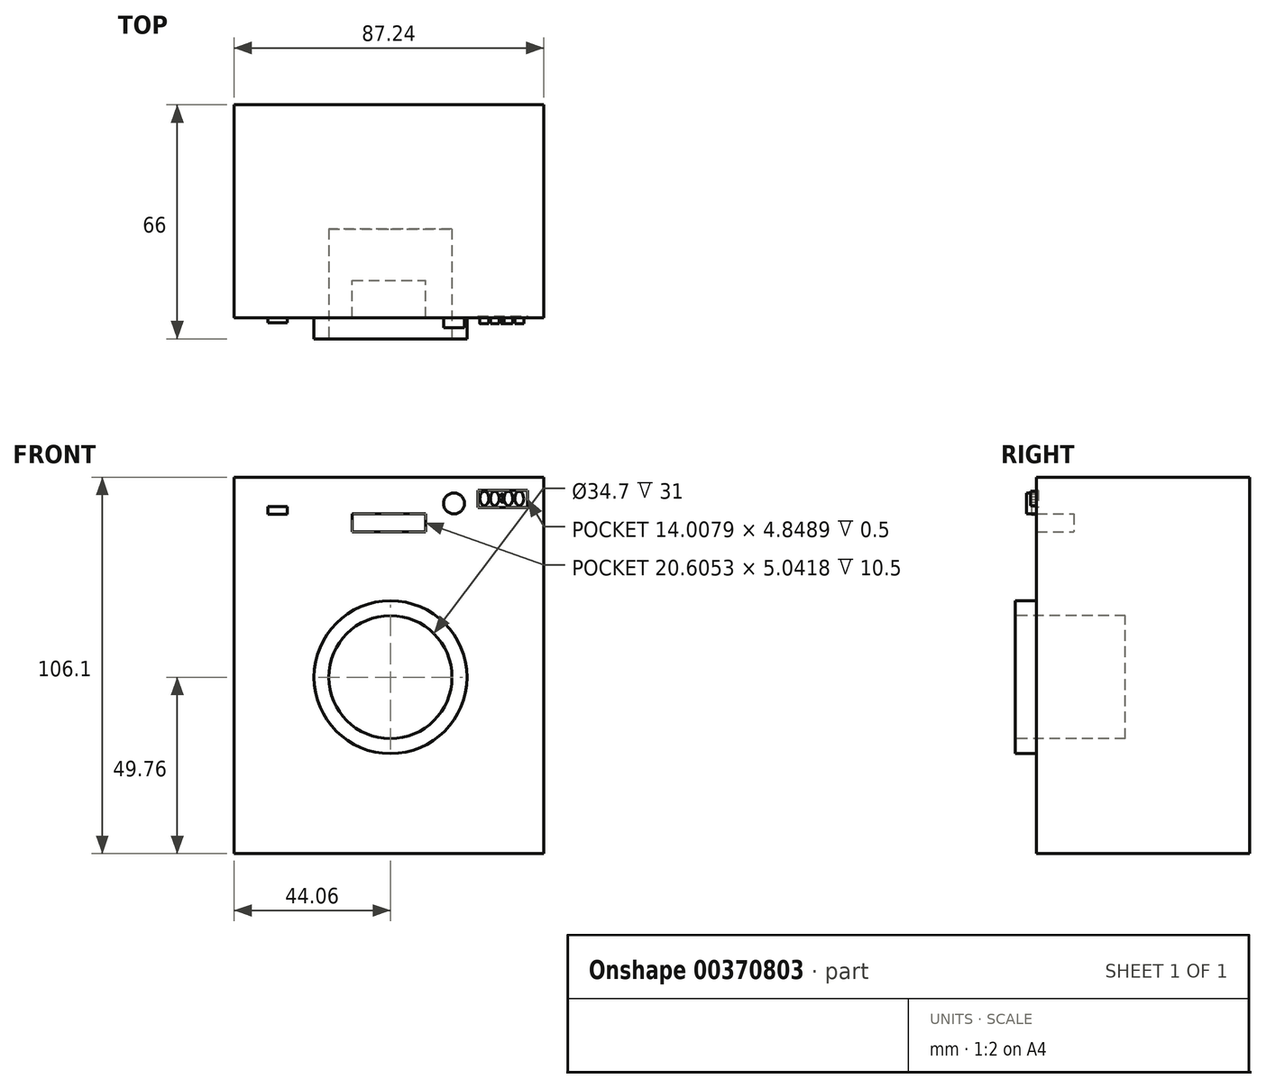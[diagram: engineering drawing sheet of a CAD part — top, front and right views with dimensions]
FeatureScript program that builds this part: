
annotation { "Feature Type Name" : "Feature", "Feature Type Description" : "" }
export const myFeature = defineFeature(function(context is Context, id is Id, definition is map)
    precondition{}
    {
        {
            var Q0;
            Q0=qCreatedBy(makeId("Front.planeOp"),FACE);
            var sketch = newSketch(context, id + "F0", { "sketchPlane" : qUnion([Q0])});
            skLineSegment(sketch, "E0.bottom", {"start": v(-44.06, 56.34) * mm, "end": v(43.18, 56.34) * mm});
            skLineSegment(sketch, "E0.top", {"start": v(-44.06, -49.76) * mm, "end": v(43.18, -49.76) * mm});
            skLineSegment(sketch, "E0.left", {"start": v(-44.06, 56.34) * mm, "end": v(-44.06, -49.76) * mm});
            skLineSegment(sketch, "E0.right", {"start": v(43.18, 56.34) * mm, "end": v(43.18, -49.76) * mm});
            skLineSegment(sketch, "E1.bottom", {"start": v(-10.74, 46.03) * mm, "end": v(9.86, 46.03) * mm});
            skLineSegment(sketch, "E1.top", {"start": v(-10.74, 41) * mm, "end": v(9.86, 41) * mm});
            skLineSegment(sketch, "E1.left", {"start": v(-10.74, 46.03) * mm, "end": v(-10.74, 41) * mm});
            skLineSegment(sketch, "E1.right", {"start": v(9.86, 46.03) * mm, "end": v(9.86, 41) * mm});
            skSolve(sketch);
        }
        {
            var Q0;
            Q0=makeQuery(id+"F0.imprint","IMPRINT",FACE,{"disambiguationData":[TD([[makeQuery(id+"F0.imprint","IMPRINT",EDGE,{"derivedFrom":sQuery(id+"F0.wireOp",EDGE,"E0.bottom")}),-1.0]])]});
            extrude(context, id + "F1", {"entities" : qUnion([Q0]), "depth" : 60 * mm});
        }
        {
            var Q0;
            Q0=makeQuery(id+"F1.opExtrude","CAP_FACE",FACE,{"disambiguationData":[OSD([sQuery(id+"F0.wireOp",EDGE,"E0.bottom"),sQuery(id+"F0.wireOp",EDGE,"E0.top"),sQuery(id+"F0.wireOp",EDGE,"E0.left"),sQuery(id+"F0.wireOp",EDGE,"E0.right"),sQuery(id+"F0.wireOp",EDGE,"E1.bottom"),sQuery(id+"F0.wireOp",EDGE,"E1.top"),sQuery(id+"F0.wireOp",EDGE,"E1.left"),sQuery(id+"F0.wireOp",EDGE,"E1.right")])],"isStart":false});
            var sketch = newSketch(context, id + "F2", { "sketchPlane" : qUnion([Q0])});
            skCircle(sketch, "E2", {"center": v(17.9, 48.98) * mm, "radius": 2.94 * mm});
            skSolve(sketch);
        }
        {
            var Q0;
            Q0=makeQuery(id+"F2.imprint","IMPRINT",FACE,{"disambiguationData":[TD([[makeQuery(id+"F2.imprint","IMPRINT",EDGE,{"derivedFrom":sQuery(id+"F2.wireOp",EDGE,"E2")}),1.0]])]});
            extrude(context, id + "F3", {"entities" : qUnion([Q0]), "operationType" : NewBodyOperationType.ADD, "depth" : 2.9 * mm});
        }
        {
            var Q0;
            Q0=makeQuery(id+"F1.opExtrude","CAP_FACE",FACE,{"disambiguationData":[OSD([sQuery(id+"F0.wireOp",EDGE,"E0.bottom"),sQuery(id+"F0.wireOp",EDGE,"E0.top"),sQuery(id+"F0.wireOp",EDGE,"E0.left"),sQuery(id+"F0.wireOp",EDGE,"E0.right"),sQuery(id+"F0.wireOp",EDGE,"E1.bottom"),sQuery(id+"F0.wireOp",EDGE,"E1.top"),sQuery(id+"F0.wireOp",EDGE,"E1.left"),sQuery(id+"F0.wireOp",EDGE,"E1.right")])],"isStart":false});
            var sketch = newSketch(context, id + "F4", { "sketchPlane" : qUnion([Q0])});
            skLineSegment(sketch, "E3.bottom", {"start": v(24.38, 52.64) * mm, "end": v(38.19, 52.64) * mm});
            skLineSegment(sketch, "E3.top", {"start": v(24.38, 48.33) * mm, "end": v(38.19, 48.33) * mm});
            skLineSegment(sketch, "E3.left", {"start": v(24.38, 52.64) * mm, "end": v(24.38, 48.33) * mm});
            skLineSegment(sketch, "E3.right", {"start": v(38.19, 52.64) * mm, "end": v(38.19, 48.33) * mm});
            skSolve(sketch);
        }
        {
            var Q0;
            Q0=makeQuery(id+"F4.imprint","IMPRINT",FACE,{"disambiguationData":[TD([[makeQuery(id+"F4.imprint","IMPRINT",EDGE,{"derivedFrom":sQuery(id+"F4.wireOp",EDGE,"E3.bottom")}),-1.0]])]});
            extrude(context, id + "F5", {"entities" : qUnion([Q0]), "operationType" : NewBodyOperationType.ADD, "oppositeDirection" : true, "depth" : 0.7 * mm});
        }
        {
            var Q0;
            Q0=makeQuery(id+"F1.opExtrude","CAP_FACE",FACE,{"disambiguationData":[OSD([sQuery(id+"F0.wireOp",EDGE,"E0.bottom"),sQuery(id+"F0.wireOp",EDGE,"E0.top"),sQuery(id+"F0.wireOp",EDGE,"E0.left"),sQuery(id+"F0.wireOp",EDGE,"E0.right"),sQuery(id+"F0.wireOp",EDGE,"E1.bottom"),sQuery(id+"F0.wireOp",EDGE,"E1.top"),sQuery(id+"F0.wireOp",EDGE,"E1.left"),sQuery(id+"F0.wireOp",EDGE,"E1.right")])],"isStart":false});
            var sketch = newSketch(context, id + "F6", { "sketchPlane" : qUnion([Q0])});
            skLineSegment(sketch, "E4.bottom", {"start": v(24.38, 52.64) * mm, "end": v(37.1, 52.64) * mm});
            skLineSegment(sketch, "E4.top", {"start": v(24.38, 47.9) * mm, "end": v(37.1, 47.9) * mm});
            skLineSegment(sketch, "E4.left", {"start": v(24.38, 52.64) * mm, "end": v(24.38, 47.9) * mm});
            skLineSegment(sketch, "E4.right", {"start": v(37.1, 52.64) * mm, "end": v(37.1, 47.9) * mm});
            skSolve(sketch);
        }
        {
            var Q0;
            Q0=makeQuery(id+"F6.imprint","IMPRINT",FACE,{"disambiguationData":[TD([[makeQuery(id+"F6.imprint","IMPRINT",EDGE,{"derivedFrom":sQuery(id+"F6.wireOp",EDGE,"E4.bottom")}),-1.0]])]});
            extrude(context, id + "F7", {"entities" : qUnion([Q0]), "operationType" : NewBodyOperationType.ADD, "oppositeDirection" : true, "depth" : 1.8 * mm});
        }
        {
            var Q0;
            Q0=makeQuery(id+"F1.opExtrude","CAP_FACE",FACE,{"disambiguationData":[OSD([sQuery(id+"F0.wireOp",EDGE,"E0.bottom"),sQuery(id+"F0.wireOp",EDGE,"E0.top"),sQuery(id+"F0.wireOp",EDGE,"E0.left"),sQuery(id+"F0.wireOp",EDGE,"E0.right"),sQuery(id+"F0.wireOp",EDGE,"E1.bottom"),sQuery(id+"F0.wireOp",EDGE,"E1.top"),sQuery(id+"F0.wireOp",EDGE,"E1.left"),sQuery(id+"F0.wireOp",EDGE,"E1.right")])],"isStart":false});
            var sketch = newSketch(context, id + "F8", { "sketchPlane" : qUnion([Q0])});
            skLineSegment(sketch, "E5.bottom", {"start": v(24.6, 52.7) * mm, "end": v(38.61, 52.7) * mm});
            skLineSegment(sketch, "E5.top", {"start": v(24.6, 47.86) * mm, "end": v(38.61, 47.86) * mm});
            skLineSegment(sketch, "E5.left", {"start": v(24.6, 52.7) * mm, "end": v(24.6, 47.86) * mm});
            skLineSegment(sketch, "E5.right", {"start": v(38.61, 52.7) * mm, "end": v(38.61, 47.86) * mm});
            skSolve(sketch);
        }
        {
            var Q0;
            Q0=makeQuery(id+"F8.imprint","IMPRINT",FACE,{"disambiguationData":[TD([[makeQuery(id+"F8.imprint","IMPRINT",EDGE,{"derivedFrom":makeQuery(id+"F1.opExtrude","CAP_EDGE",EDGE,{"disambiguationData":[OSD([sQuery(id+"F0.wireOp",EDGE,"E1.bottom")])],"isStart":false})}),-1.0]])]});
            extrude(context, id + "F9", {"entities" : qUnion([Q0]), "operationType" : NewBodyOperationType.REMOVE, "oppositeDirection" : true, "depth" : 5.2 * mm});
        }
        {
            var Q0;
            Q0=makeQuery(id+"F8.imprint","IMPRINT",FACE,{"disambiguationData":[TD([[makeQuery(id+"F8.imprint","IMPRINT",EDGE,{"derivedFrom":sQuery(id+"F8.wireOp",EDGE,"E5.bottom")}),-1.0]])]});
            extrude(context, id + "F10", {"entities" : qUnion([Q0]), "operationType" : NewBodyOperationType.REMOVE, "oppositeDirection" : true, "depth" : 0.5 * mm});
        }
        {
            var Q0;
            Q0=makeQuery(id+"F8.imprint","IMPRINT",FACE,{"disambiguationData":[TD([[makeQuery(id+"F8.imprint","IMPRINT",EDGE,{"derivedFrom":sQuery(id+"F8.wireOp",EDGE,"E5.bottom")}),1.0]])]});
            var sketch = newSketch(context, id + "F11", { "sketchPlane" : qUnion([Q0])});
            skLineSegment(sketch, "E6.bottom", {"start": v(-34.48, 48.04) * mm, "end": v(-29.1, 48.04) * mm});
            skLineSegment(sketch, "E6.top", {"start": v(-34.48, 45.89) * mm, "end": v(-29.1, 45.89) * mm});
            skLineSegment(sketch, "E6.left", {"start": v(-34.48, 48.04) * mm, "end": v(-34.48, 45.89) * mm});
            skLineSegment(sketch, "E6.right", {"start": v(-29.1, 48.04) * mm, "end": v(-29.1, 45.89) * mm});
            skSolve(sketch);
        }
        {
            var Q0;
            Q0 = qSketchRegion(id + "F11", true);
            extrude(context, id + "F12", {"entities" : qUnion([Q0]), "operationType" : NewBodyOperationType.ADD, "depth" : 1.4 * mm});
        }
        {
            var Q0;
            Q0=makeQuery(id+"F8.imprint","IMPRINT",FACE,{"disambiguationData":[TD([[makeQuery(id+"F8.imprint","IMPRINT",EDGE,{"derivedFrom":sQuery(id+"F8.wireOp",EDGE,"E5.bottom")}),1.0]])]});
            var sketch = newSketch(context, id + "F13", { "sketchPlane" : qUnion([Q0])});
            skCircle(sketch, "E7", {"center": v(0, 0) * mm, "radius": 21.55 * mm});
            skCircle(sketch, "E8", {"center": v(0, 0) * mm, "radius": 17.35 * mm});
            skSolve(sketch);
        }
        {
            var Q0;
            Q0=makeQuery(id+"F13.imprint","IMPRINT",FACE,{"disambiguationData":[TD([[makeQuery(id+"F13.imprint","IMPRINT",EDGE,{"derivedFrom":sQuery(id+"F13.wireOp",EDGE,"E8")}),1.0]])]});
            extrude(context, id + "F14", {"entities" : qUnion([Q0]), "operationType" : NewBodyOperationType.REMOVE, "oppositeDirection" : true, "depth" : 25 * mm});
        }
        {
            var Q0;
            Q0 = qSketchRegion(id + "F13", true);
            extrude(context, id + "F15", {"entities" : qUnion([Q0]), "operationType" : NewBodyOperationType.ADD, "depth" : 6 * mm});
        }
        {
            var Q0;
            Q0=makeQuery(id+"F1.opExtrude","CAP_FACE",FACE,{"disambiguationData":[OSD([sQuery(id+"F0.wireOp",EDGE,"E0.bottom"),sQuery(id+"F0.wireOp",EDGE,"E0.top"),sQuery(id+"F0.wireOp",EDGE,"E0.left"),sQuery(id+"F0.wireOp",EDGE,"E0.right"),sQuery(id+"F0.wireOp",EDGE,"E1.bottom"),sQuery(id+"F0.wireOp",EDGE,"E1.top"),sQuery(id+"F0.wireOp",EDGE,"E1.left"),sQuery(id+"F0.wireOp",EDGE,"E1.right")])],"isStart":true});
            var sketch = newSketch(context, id + "F16", { "sketchPlane" : qUnion([Q0])});
            skLineSegment(sketch, "E9.bottom", {"start": v(-9.86, 46.03) * mm, "end": v(10.74, 46.03) * mm});
            skLineSegment(sketch, "E9.top", {"start": v(-9.86, 41) * mm, "end": v(10.74, 41) * mm});
            skLineSegment(sketch, "E9.left", {"start": v(-9.86, 46.03) * mm, "end": v(-9.86, 41) * mm});
            skLineSegment(sketch, "E9.right", {"start": v(10.74, 46.03) * mm, "end": v(10.74, 41) * mm});
            skSolve(sketch);
        }
        {
            var Q0;
            Q0=makeQuery(id+"F16.imprint","IMPRINT",FACE,{"disambiguationData":[TD([[makeQuery(id+"F16.imprint","IMPRINT",EDGE,{"derivedFrom":sQuery(id+"F16.wireOp",EDGE,"E9.bottom")}),1.0]])]});
            extrude(context, id + "F17", {"entities" : qUnion([Q0]), "operationType" : NewBodyOperationType.ADD, "oppositeDirection" : true, "depth" : 49.5 * mm});
        }
        {
            var Q0;
            Q0=makeQuery(id+"F8.imprint","IMPRINT",FACE,{"disambiguationData":[TD([[makeQuery(id+"F8.imprint","IMPRINT",EDGE,{"derivedFrom":sQuery(id+"F8.wireOp",EDGE,"E5.bottom")}),-1.0]])]});
            var sketch = newSketch(context, id + "F18", { "sketchPlane" : qUnion([Q0])});
            skEllipse(sketch, "E10", {"center": v(26.47, 50.38) * mm, "majorRadius": 2 * mm, "minorRadius": 1.26 * mm, "majorAxis": v(0, 1)});
            skEllipse(sketch, "E11", {"center": v(29.4, 50.38) * mm, "majorRadius": 2 * mm, "minorRadius": 1.24 * mm, "majorAxis": v(0, 1)});
            skCircle(sketch, "E12", {"center": v(31.48, 51.24) * mm, "radius": 0.4 * mm});
            skCircle(sketch, "E13", {"center": v(31.48, 49.7) * mm, "radius": 0.4 * mm});
            skEllipse(sketch, "E14", {"center": v(33.23, 50.38) * mm, "majorRadius": 2 * mm, "minorRadius": 1.24 * mm, "majorAxis": v(0, 1)});
            skEllipse(sketch, "E15", {"center": v(36.3, 50.38) * mm, "majorRadius": 2 * mm, "minorRadius": 1.26 * mm, "majorAxis": v(0, 1)});
            skSolve(sketch);
        }
        {
            var Q0;
            Q0 = qSketchRegion(id + "F18", true);
            extrude(context, id + "F19", {"entities" : qUnion([Q0]), "depth" : 1.7 * mm});
        }
    });
